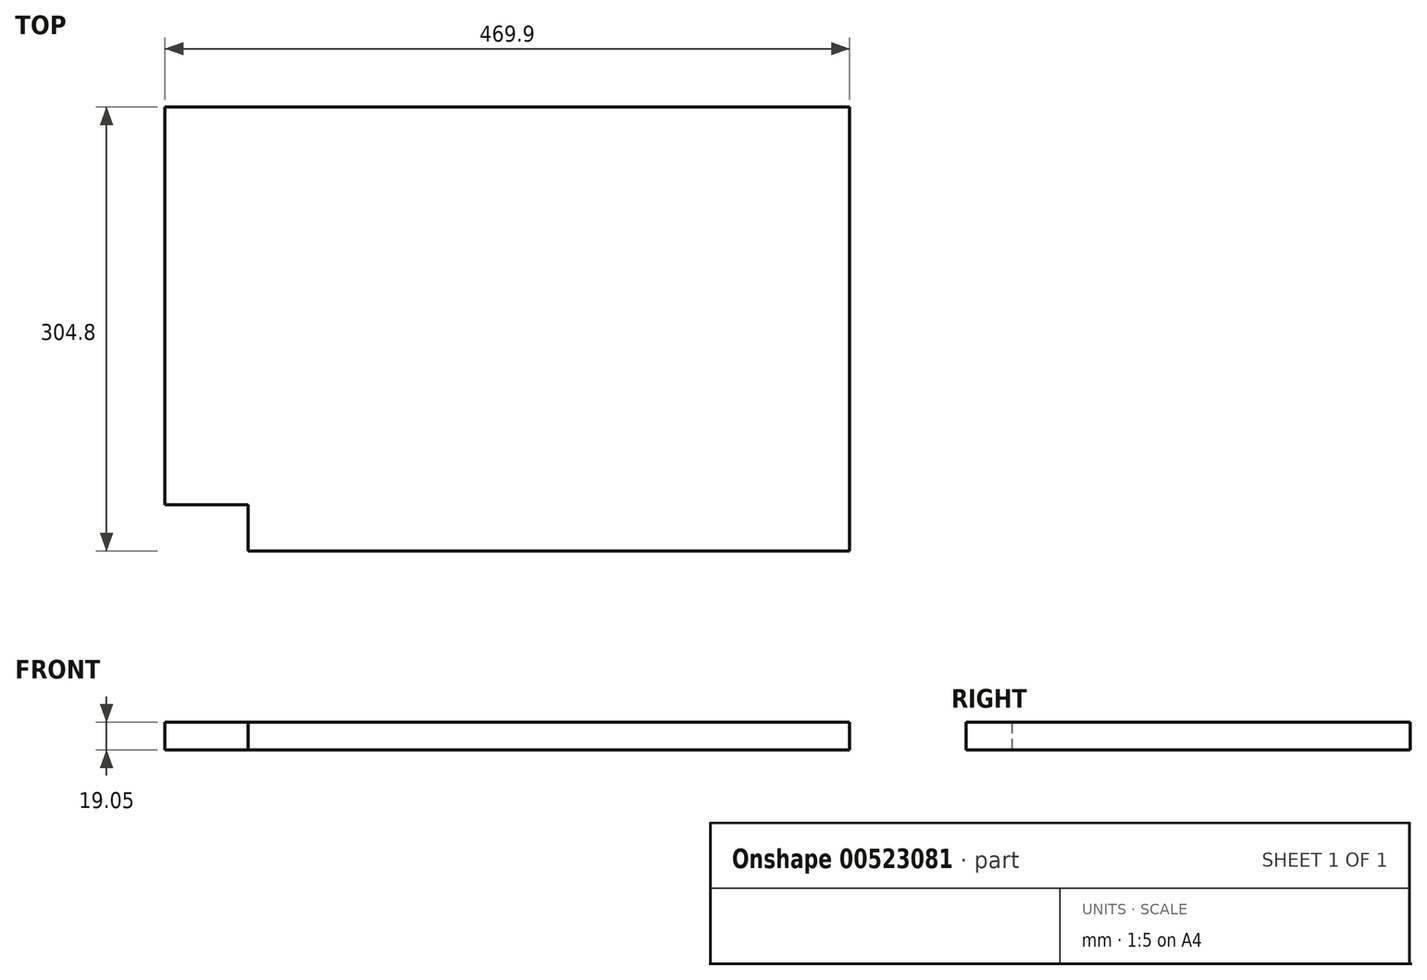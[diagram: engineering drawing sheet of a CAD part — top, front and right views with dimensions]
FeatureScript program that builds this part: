
annotation { "Feature Type Name" : "Feature", "Feature Type Description" : "" }
export const myFeature = defineFeature(function(context is Context, id is Id, definition is map)
    precondition{}
    {
        {
            var Q0;
            Q0=qCreatedBy(makeId("Top.planeOp"),FACE);
            var sketch = newSketch(context, id + "F0", { "sketchPlane" : qUnion([Q0])});
            skLineSegment(sketch, "E0.bottom", {"start": v(0, 0) * mm, "end": v(469.9, 0) * mm});
            skLineSegment(sketch, "E0.top", {"start": v(0, 304.8) * mm, "end": v(469.9, 304.8) * mm});
            skLineSegment(sketch, "E0.left", {"start": v(0, 0) * mm, "end": v(0, 304.8) * mm});
            skLineSegment(sketch, "E0.right", {"start": v(469.9, 0) * mm, "end": v(469.9, 304.8) * mm});
            skSolve(sketch);
        }
        {
            var Q0;
            Q0 = qSketchRegion(id + "F0", true);
            extrude(context, id + "F1", {"entities" : qUnion([Q0]), "depth" : 19.05 * mm, "offsetDistance" : 25.4 * mm});
        }
        {
            var Q0;
            Q0=makeQuery(id+"F1.opExtrude","CAP_FACE",FACE,{"disambiguationData":[OSD([sQuery(id+"F0.wireOp",EDGE,"E0.bottom"),sQuery(id+"F0.wireOp",EDGE,"E0.top"),sQuery(id+"F0.wireOp",EDGE,"E0.left"),sQuery(id+"F0.wireOp",EDGE,"E0.right")])],"isStart":false});
            var sketch = newSketch(context, id + "F2", { "sketchPlane" : qUnion([Q0])});
            skLineSegment(sketch, "E1.bottom", {"start": v(0, 0) * mm, "end": v(57.15, 0) * mm});
            skLineSegment(sketch, "E1.top", {"start": v(0, 31.75) * mm, "end": v(57.15, 31.75) * mm});
            skLineSegment(sketch, "E1.left", {"start": v(0, 0) * mm, "end": v(0, 31.75) * mm});
            skLineSegment(sketch, "E1.right", {"start": v(57.15, 0) * mm, "end": v(57.15, 31.75) * mm});
            skSolve(sketch);
        }
        {
            var Q0;
            Q0 = qSketchRegion(id + "F2", true);
            extrude(context, id + "F3", {"entities" : qUnion([Q0]), "operationType" : NewBodyOperationType.REMOVE, "endBound" : BoundingType.THROUGH_ALL, "oppositeDirection" : true, "depth" : 25.4 * mm, "offsetDistance" : 25.4 * mm});
        }
    });
